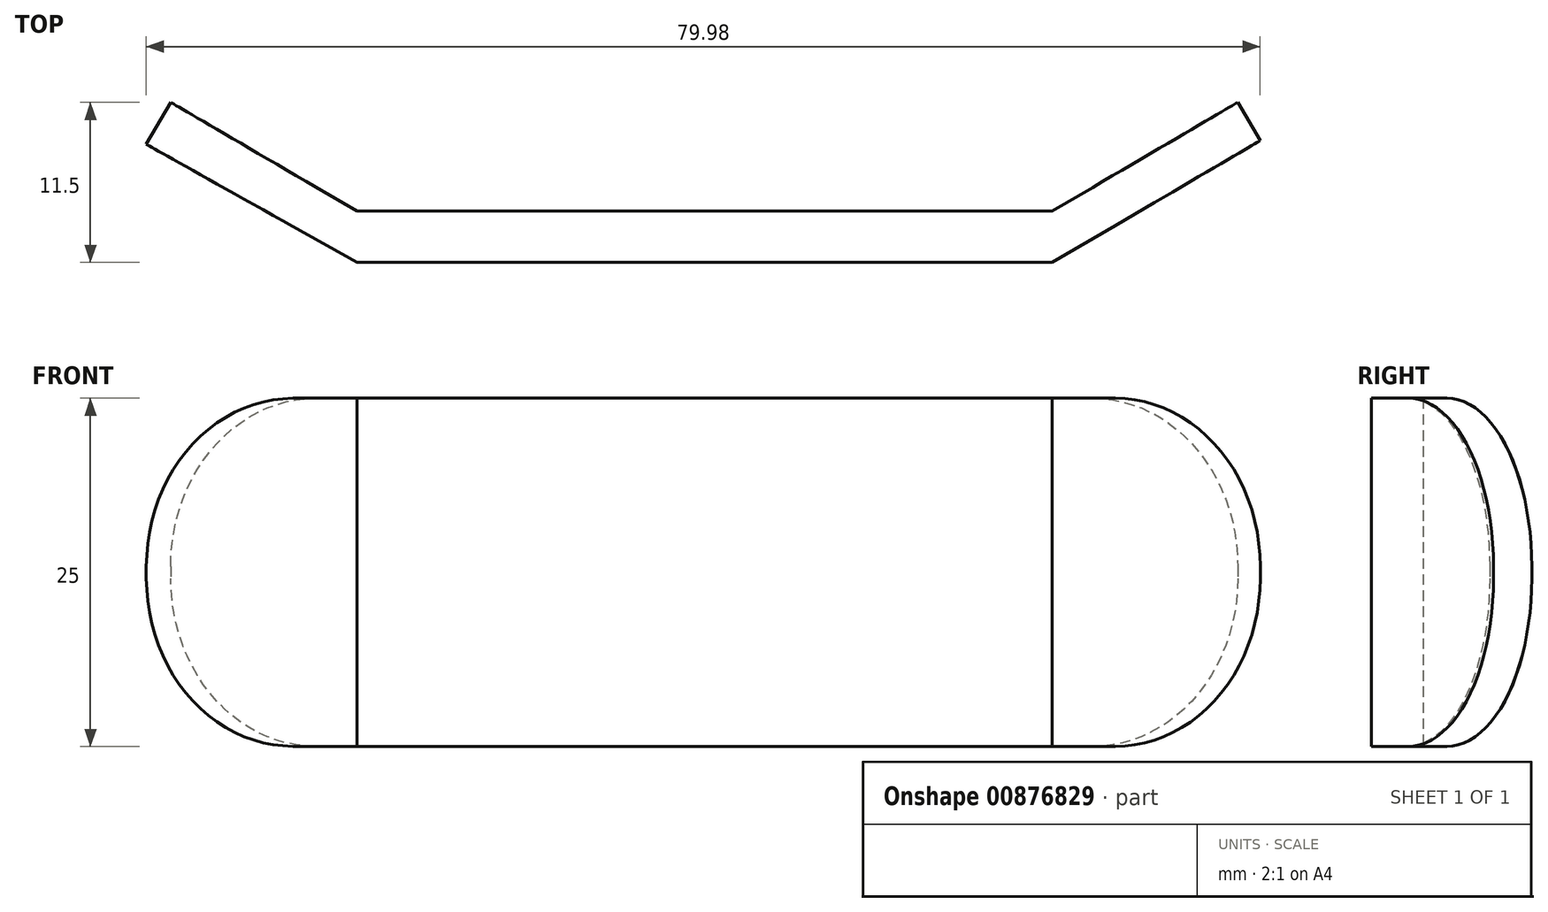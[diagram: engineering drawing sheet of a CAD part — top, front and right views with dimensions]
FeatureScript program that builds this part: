
annotation { "Feature Type Name" : "Feature", "Feature Type Description" : "" }
export const myFeature = defineFeature(function(context is Context, id is Id, definition is map)
    precondition{}
    {
        {
            var Q0;
            Q0=qCreatedBy(makeId("Top.planeOp"),FACE);
            var sketch = newSketch(context, id + "F0", { "sketchPlane" : qUnion([Q0])});
            skLineSegment(sketch, "E0", {"start": v(-60.16, 15.32) * mm, "end": v(-58.4, 18.34) * mm});
            skLineSegment(sketch, "E1", {"start": v(-58.4, 18.34) * mm, "end": v(-45.02, 10.53) * mm});
            skLineSegment(sketch, "E2", {"start": v(-45.02, 10.53) * mm, "end": v(4.9, 10.53) * mm});
            skLineSegment(sketch, "E3", {"start": v(4.9, 10.53) * mm, "end": v(18.21, 18.34) * mm});
            skLineSegment(sketch, "E4", {"start": v(18.21, 18.34) * mm, "end": v(19.82, 15.6) * mm});
            skLineSegment(sketch, "E5", {"start": v(19.82, 15.6) * mm, "end": v(4.9, 6.84) * mm});
            skLineSegment(sketch, "E6", {"start": v(4.9, 6.84) * mm, "end": v(-45.02, 6.84) * mm});
            skLineSegment(sketch, "E7", {"start": v(-45.02, 6.84) * mm, "end": v(-60.16, 15.32) * mm});
            skSolve(sketch);
        }
        {
            var Q0;
            Q0=qSketchRegion(id+"F0",true);
            extrude(context, id + "F1", {"entities" : qUnion([Q0]), "depth" : 25 * mm, "offsetDistance" : 25 * mm});
        }
        {
            var Q0;
            Q0=makeQuery(id+"F1.opExtrude","CAP_EDGE",EDGE,{"disambiguationData":[OSD([sQuery(id+"F0.wireOp",EDGE,"E0")])],"isStart":false});
            var Q1;
            Q1=makeQuery(id+"F1.opExtrude","CAP_EDGE",EDGE,{"disambiguationData":[OSD([sQuery(id+"F0.wireOp",EDGE,"E0")])],"isStart":true});
            var Q2;
            Q2=makeQuery(id+"F1.opExtrude","CAP_EDGE",EDGE,{"disambiguationData":[OSD([sQuery(id+"F0.wireOp",EDGE,"E4")])],"isStart":false});
            var Q3;
            Q3=makeQuery(id+"F1.opExtrude","CAP_EDGE",EDGE,{"disambiguationData":[OSD([sQuery(id+"F0.wireOp",EDGE,"E4")])],"isStart":true});
            fillet(context, id + "F2", {"entities" : qUnion([Q0, Q1, Q2, Q3]), "radius" : 12.07 * mm, "tangentPropagation" : true, "allowEdgeOverflow" : false});
        }
    });
